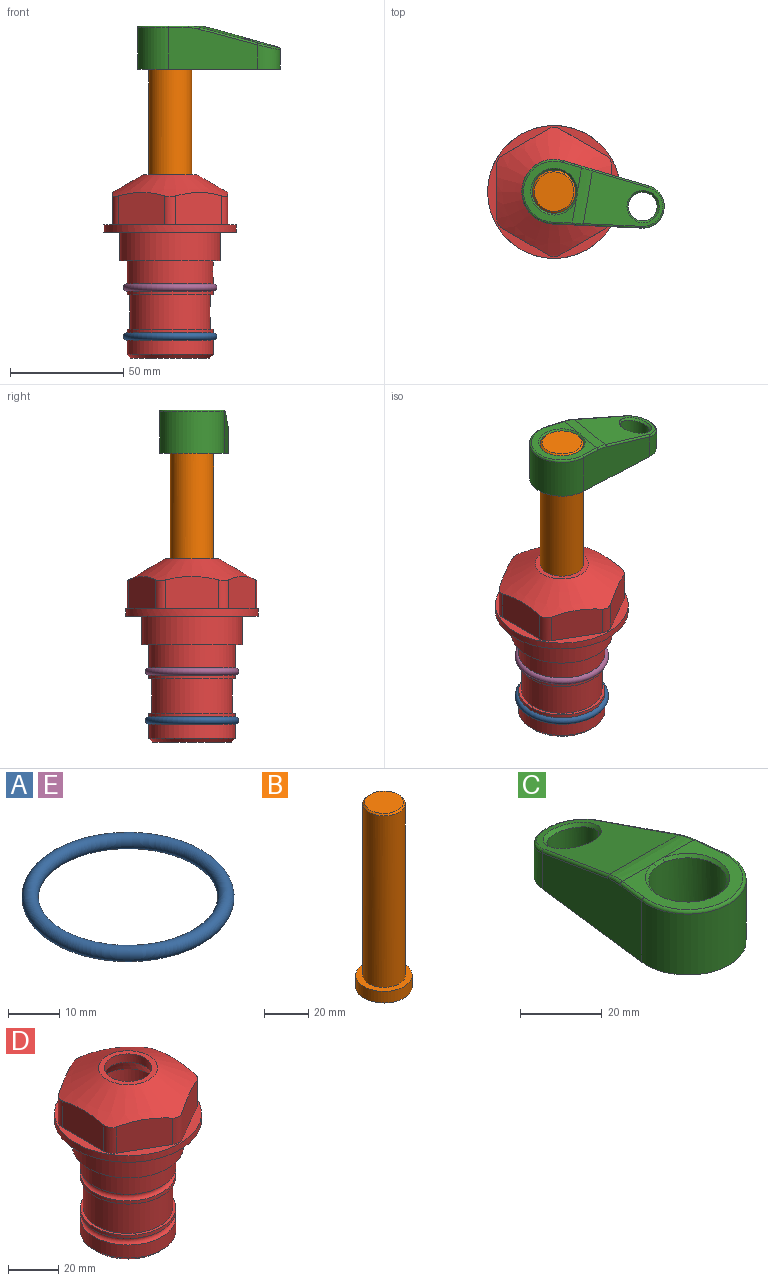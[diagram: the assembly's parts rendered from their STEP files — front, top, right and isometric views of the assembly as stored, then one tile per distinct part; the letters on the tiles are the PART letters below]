
ASSEMBLY  parts=5 mates=4
PART A: 1 faces, bbox 44.7x44.7x3.2 mm
  f0: torus R=19.05mm, axis (0,0,1), area 1193.9mm2
PART B: 6 faces, bbox 25.4x25.4x101.6 mm
  f0: plane 17.46x17.46mm, normal (0,0,1), area 239.5mm2, adj f5
  f1: plane 25.4x25.4mm, normal (0,0,-1), area 506.7mm2, adj f2
  f2: cylinder r=12.7mm len=25.4mm, axis (0,0,1), area 506.7mm2, adj f1,f3
  f3: plane 25.4x25.4mm, normal (0,0,1), area 221.7mm2, adj f2,f4
  f4: cylinder r=9.53mm len=94.46mm, axis (0,0,1), area 5653mm2, adj f3,f5
  f5: cone r=8.73mm half-angle=45deg, axis (0,0,-1), area 64.4mm2, adj f0,f4
PART C: 31 faces, bbox 31.7x65.5x19.8 mm
  f0: plane 39.12x18.26mm, normal (0.99,0.12,0), area 612.2mm2, adj f1,f4,f7,f11,f13,f15
  f1: cylinder r=9.53mm len=18.91mm, axis (0,0,-1), area 296.1mm2, adj f0,f2,f7,f17
  f2: plane 39.12x18.26mm, normal (-0.99,0.12,0), area 612.2mm2, adj f1,f4,f7,f12,f14,f16
  f3: cylinder r=6.35mm len=12.7mm, axis (0,0,-1), area 362.4mm2, adj f7,f18
  f4: cylinder r=14.29mm len=28.58mm, axis (0,0,-1), area 882.2mm2, adj f0,f2,f7,f10
  f5: cylinder r=9.53mm len=19.05mm, axis (0,0,-1), area 1092.6mm2, adj f7,f19,f20
  f6: plane 26.99x23.69mm, normal (0,0,1), area 216.2mm2, adj f9,f10,f11,f12,f19
  f7: plane 63.5x28.58mm, normal (0,0,-1), area 661.8mm2, adj f0,f1,f2,f3,f4,f5,f22,f23
  f8: plane 33.52x23.6mm, normal (0,0.26,0.97), area 486mm2, adj f9,f15,f16,f17,f18
  f9: cylinder r=19.05mm len=24.72mm, axis (1,0,0), area 120.4mm2, adj f6,f8,f13,f14,f20
  f10: torus R=13.49mm, axis (0,0,1), area 59mm2, adj f4,f6,f11,f12
  f11: cylinder r=0.79mm len=8.67mm, axis (0.12,-0.99,0), area 10.8mm2, adj f0,f6,f10,f13
  f12: cylinder r=0.79mm len=8.67mm, axis (0.12,0.99,0), area 10.8mm2, adj f2,f6,f10,f14
  f13: bspline ~4.95x1.42mm, area 6.1mm2, adj f0,f9,f11,f15
  f14: bspline ~4.95x1.42mm, area 6.1mm2, adj f2,f9,f12,f16
  f15: cylinder r=0.79mm len=25.95mm, axis (0.12,-0.96,0.26), area 32.9mm2, adj f0,f8,f13,f17
  f16: cylinder r=0.79mm len=25.95mm, axis (0.12,0.96,-0.26), area 32.9mm2, adj f2,f8,f14,f17
  f17: bspline ~18.91x8.38mm, area 30mm2, adj f1,f8,f15,f16
  f18: bspline ~14.29x14.29mm, area 48.3mm2, adj f3,f8
  f19: cone r=9.53mm half-angle=45deg, axis (0,0,1), area 66.5mm2, adj f5,f6,f20
  f20: bspline ~3.22x0.96mm, area 3.5mm2, adj f5,f9,f19
  f21: plane 2.75x2.72mm, normal (0,0,-1), area 2.9mm2, adj f23,f25,f28
  f22: plane 23.05x15.88mm, normal (-0.99,-0.12,0), area 323.6mm2, adj f7,f25,f26,f27,f28,f29
  f23: plane 23.05x15.88mm, normal (0.99,-0.12,0), area 323.6mm2, adj f7,f21,f25,f27,f28,f30
  f24: cylinder r=9.53mm len=10.69mm, axis (0,0,-1), area 114.7mm2, adj f7,f27,f29,f30
  f25: cylinder r=12.7mm len=20.59mm, axis (0,0,-1), area 381.1mm2, adj f7,f21,f22,f23,f26,f28
  f26: plane 2.75x2.72mm, normal (0,0,-1), area 2.9mm2, adj f22,f25,f28
  f27: plane 19.72x18.37mm, normal (0,-0.26,-0.97), area 291.8mm2, adj f22,f23,f24,f28,f29,f30
  f28: cylinder r=15.88mm len=19.92mm, axis (1,0,0), area 54.8mm2, adj f21,f22,f23,f25,f26,f27
  f29: cylinder r=1.59mm len=11mm, axis (0,0,-1), area 34.7mm2, adj f7,f22,f24,f27
  f30: cylinder r=1.59mm len=11mm, axis (0,0,-1), area 34.7mm2, adj f7,f23,f24,f27
PART D: 36 faces, bbox 58.7x58.7x81 mm
  f0: cylinder r=17.78mm len=35.56mm, axis (0,0,1), area 1670.8mm2, adj f23,f24,f31
  f1: cylinder r=19.05mm len=38.1mm, axis (0,0,1), area 1191.9mm2, adj f26,f27,f30
  f2: plane 58.66x58.66mm, normal (0,0,-1), area 1150.6mm2, adj f3,f28
  f3: cylinder r=29.33mm len=58.66mm, axis (0,0,-1), area 585.1mm2, adj f2,f4
  f4: plane 58.66x58.66mm, normal (0,0,1), area 475.9mm2, adj f3,f5,f6,f7,f8,f9,f10,f11
  f5: plane 20.32x14.34mm, normal (-0.5,0.87,0), area 324.4mm2, adj f4,f15,f16,f17
  f6: plane 20.32x14.34mm, normal (0.5,0.87,0), area 324.4mm2, adj f4,f14,f15,f17
  f7: plane 23.48x14.34mm, normal (1,0,0), area 324.4mm2, adj f4,f13,f14,f17
  f8: plane 20.32x14.34mm, normal (0.5,-0.87,0), area 324.4mm2, adj f4,f12,f13,f17
  f9: plane 20.32x14.34mm, normal (-0.5,-0.87,0), area 324.4mm2, adj f4,f11,f12,f17
  f10: plane 23.48x14.34mm, normal (-1,0,0), area 324.4mm2, adj f4,f11,f16,f17
  f11: cylinder r=5.08mm len=12.85mm, axis (0,0,-1), area 67.2mm2, adj f4,f9,f10,f17
  f12: cylinder r=5.08mm len=12.85mm, axis (0,0,-1), area 67.2mm2, adj f4,f8,f9,f17
  f13: cylinder r=5.08mm len=12.85mm, axis (0,0,-1), area 67.2mm2, adj f4,f7,f8,f17
  f14: cylinder r=5.08mm len=12.85mm, axis (0,0,-1), area 67.2mm2, adj f4,f6,f7,f17
  f15: cylinder r=5.08mm len=12.85mm, axis (0,0,-1), area 67.2mm2, adj f4,f5,f6,f17
  f16: cylinder r=5.08mm len=12.85mm, axis (0,0,-1), area 67.2mm2, adj f4,f5,f10,f17
  f17: cone r=11.73mm half-angle=60deg, axis (0,0,-1), area 2071.8mm2, adj f5,f6,f7,f8,f9,f10,f11,f12
  f18: plane 23.46x23.46mm, normal (0,0,1), area 147.4mm2, adj f17,f35
  f19: plane 34.93x34.93mm, normal (0,0,-1), area 958mm2, adj f29
  f20: cylinder r=19.05mm len=38.1mm, axis (0,0,1), area 760.1mm2, adj f21,f29
  f21: torus R=19.05mm, axis (0,0,1), area 565.3mm2, adj f20,f22
  f22: cylinder r=19.05mm len=38.1mm, axis (0,0,1), area 190mm2, adj f21,f23
  f23: plane 38.1x38.1mm, normal (0,0,1), area 146.9mm2, adj f0,f22
  f24: plane 38.1x38.1mm, normal (0,0,-1), area 146.9mm2, adj f0,f25
  f25: cylinder r=19.05mm len=38.1mm, axis (0,0,1), area 190mm2, adj f24,f26
  f26: torus R=19.05mm, axis (0,0,1), area 565.3mm2, adj f1,f25
  f27: plane 44.45x44.45mm, normal (0,0,-1), area 411.7mm2, adj f1,f28
  f28: cylinder r=22.23mm len=44.45mm, axis (0,0,1), area 1773.5mm2, adj f2,f27
  f29: cone r=19.05mm half-angle=45deg, axis (0,0,1), area 257.5mm2, adj f19,f20
  f30: cylinder r=3.17mm len=6.75mm, axis (-1,0,0), area 128mm2, adj f1,f33
  f31: cylinder r=3.17mm len=6.35mm, axis (-1,0,0), area 102.5mm2, adj f0,f33
  f32: plane 25.4x25.4mm, normal (0,0,1), area 506.7mm2, adj f33
  f33: cylinder r=12.7mm len=66.42mm, axis (0,0,-1), area 5236.2mm2, adj f30,f31,f32,f34
  f34: cone r=9.53mm half-angle=30deg, axis (0,0,-1), area 443.4mm2, adj f33,f35
  f35: cylinder r=9.53mm len=19.05mm, axis (0,0,-1), area 240.9mm2, adj f18,f34
PART E: same geometry as A
PLACE A t=(0,0,-21.59)mm
PLACE B rot(axis=(0,0,-1),99.5deg) t=(0,0,27.55)mm
PLACE C rot(axis=(0,0,-1),99.5deg) t=(0,0,27.55)mm
PLACE D at identity fixed
PLACE E at identity
MATE fastened B.f2 <-> C.f4  axis (0,0,1) through (0,0,91.05)mm
MATE fastened A.f0 <-> D.f0  axis (0,0,1) through (0,0,-46.1)mm
MATE cylindrical B.f2 <-> D.f0  axis (0,0,-1) through (0,0,-10.55)mm
MATE fastened E.f0 <-> D.f0  axis (0,0,1) through (0,0,-24.51)mm
